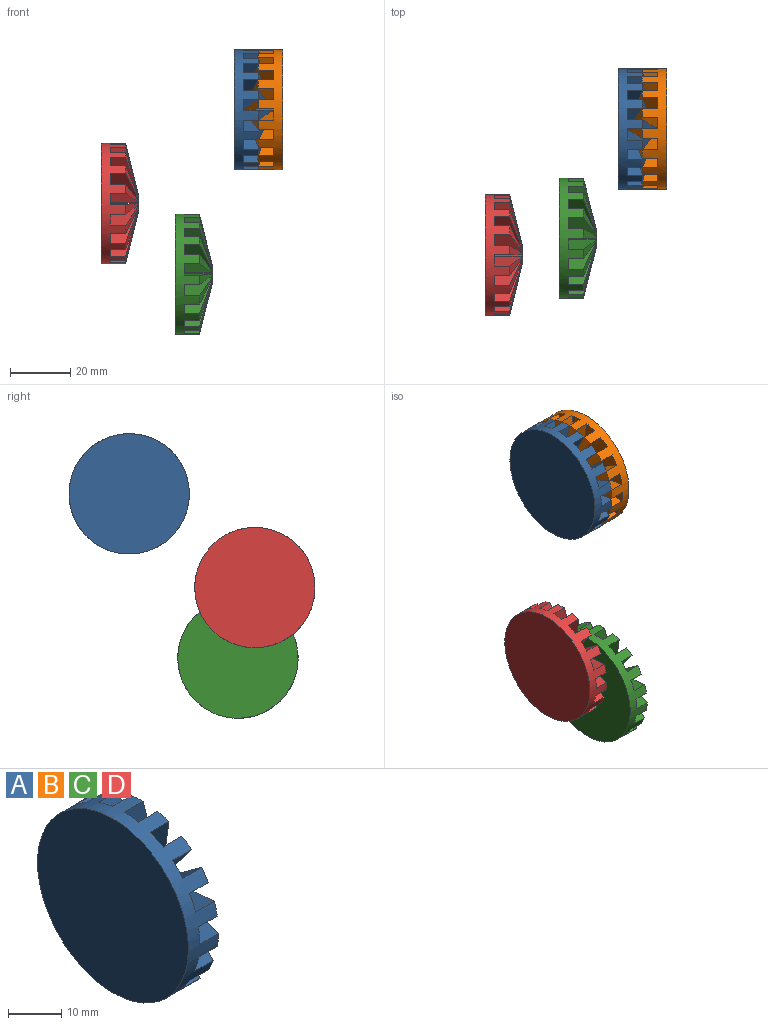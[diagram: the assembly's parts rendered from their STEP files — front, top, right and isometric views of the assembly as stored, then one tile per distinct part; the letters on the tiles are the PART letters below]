
ASSEMBLY  parts=4 mates=1
PART A: 75 faces, bbox 12.3x40x40 mm
  f0: cone r=0mm half-angle=76deg, axis (-1,0,0), area 31.7mm2, adj f18,f20,f21,f73
  f1: cone r=0mm half-angle=76deg, axis (-1,0,0), area 31.7mm2, adj f18,f22,f23,f24
  f2: cone r=0mm half-angle=76deg, axis (-1,0,0), area 31.7mm2, adj f18,f25,f26,f27
  f3: cone r=0mm half-angle=76deg, axis (-1,0,0), area 31.7mm2, adj f18,f28,f29,f30
  f4: cone r=0mm half-angle=76deg, axis (-1,0,0), area 31.7mm2, adj f18,f31,f32,f33
  f5: cone r=0mm half-angle=76deg, axis (-1,0,0), area 31.7mm2, adj f18,f34,f35,f36
  f6: cone r=0mm half-angle=76deg, axis (-1,0,0), area 31.7mm2, adj f18,f37,f38,f39
  f7: cone r=0mm half-angle=76deg, axis (-1,0,0), area 31.7mm2, adj f18,f40,f41,f42
  f8: cone r=0mm half-angle=76deg, axis (-1,0,0), area 31.7mm2, adj f18,f43,f44,f45
  f9: cone r=0mm half-angle=76deg, axis (-1,0,0), area 31.7mm2, adj f18,f46,f47,f48
  f10: cone r=0mm half-angle=76deg, axis (-1,0,0), area 31.7mm2, adj f18,f49,f50,f51
  f11: cone r=0mm half-angle=76deg, axis (-1,0,0), area 31.7mm2, adj f18,f52,f53,f54
  f12: cone r=0mm half-angle=76deg, axis (-1,0,0), area 31.7mm2, adj f18,f55,f56,f57
  f13: cone r=0mm half-angle=76deg, axis (-1,0,0), area 31.7mm2, adj f18,f58,f59,f60
  f14: cone r=0mm half-angle=76deg, axis (-1,0,0), area 31.7mm2, adj f18,f61,f62,f63
  f15: cone r=0mm half-angle=76deg, axis (-1,0,0), area 31.7mm2, adj f18,f64,f65,f66
  f16: cone r=0mm half-angle=76deg, axis (-1,0,0), area 31.7mm2, adj f18,f67,f68,f69
  f17: cone r=0mm half-angle=76deg, axis (-1,0,0), area 31.7mm2, adj f18,f70,f71,f72
  f18: cylinder r=20mm len=40mm, axis (-1,0,0), area 659.7mm2, adj f0,f1,f2,f3,f4,f5,f6,f7
  f19: plane 40x40mm, normal (-1,0,0), area 1256.6mm2, adj f18
  f20: cylinder r=3mm len=9.25mm, axis (-1,0,0), area 4.4mm2, adj f0,f21,f73,f74
  f21: plane 16.74x9.25mm, normal (0,-0.17,0.98), area 121.1mm2, adj f0,f18,f20,f74
  f22: plane 15.87x9.25mm, normal (0,0.36,-0.93), area 121.1mm2, adj f1,f18,f23,f74
  f23: cylinder r=3mm len=9.25mm, axis (-1,0,0), area 4.4mm2, adj f1,f22,f24,f74
  f24: plane 14.72x9.25mm, normal (0,-0.5,0.87), area 121.1mm2, adj f1,f18,f23,f74
  f25: plane 12.83x11.15mm, normal (0,0.66,-0.75), area 121.1mm2, adj f2,f18,f26,f74
  f26: cylinder r=3mm len=9.25mm, axis (-1,0,0), area 4.4mm2, adj f2,f25,f27,f74
  f27: plane 13.02x10.93mm, normal (0,-0.77,0.64), area 121.1mm2, adj f2,f18,f26,f74
  f28: plane 14.87x9.25mm, normal (0,0.87,-0.48), area 121.1mm2, adj f3,f18,f29,f74
  f29: cylinder r=3mm len=9.25mm, axis (-1,0,0), area 4.4mm2, adj f3,f28,f30,f74
  f30: plane 15.97x9.25mm, normal (0,-0.94,0.34), area 121.1mm2, adj f3,f18,f29,f74
  f31: plane 16.79x9.25mm, normal (0,0.99,-0.16), area 121.1mm2, adj f4,f18,f32,f74
  f32: cylinder r=3mm len=9.25mm, axis (-1,0,0), area 4.4mm2, adj f4,f31,f33,f74
  f33: plane 17x9.25mm, normal (0,-1,0), area 121.1mm2, adj f4,f18,f32,f74
  f34: plane 16.69x9.25mm, normal (0,0.98,0.19), area 121.1mm2, adj f5,f18,f35,f74
  f35: cylinder r=3mm len=9.25mm, axis (-1,0,0), area 4.4mm2, adj f5,f34,f36,f74
  f36: plane 15.97x9.25mm, normal (0,-0.94,-0.34), area 121.1mm2, adj f5,f18,f35,f74
  f37: plane 14.57x9.25mm, normal (0,0.86,0.52), area 121.1mm2, adj f6,f18,f38,f74
  f38: cylinder r=3mm len=9.25mm, axis (-1,0,0), area 4.4mm2, adj f6,f37,f39,f74
  f39: plane 13.02x10.93mm, normal (0,-0.77,-0.64), area 121.1mm2, adj f6,f18,f38,f74
  f40: plane 13.21x10.7mm, normal (0,0.63,0.78), area 121.1mm2, adj f7,f18,f41,f74
  f41: cylinder r=3mm len=9.25mm, axis (-1,0,0), area 4.4mm2, adj f7,f40,f42,f74
  f42: plane 14.72x9.25mm, normal (0,-0.5,-0.87), area 121.1mm2, adj f7,f18,f41,f74
  f43: plane 16.07x9.25mm, normal (0,0.33,0.95), area 121.1mm2, adj f8,f18,f44,f74
  f44: cylinder r=3mm len=9.25mm, axis (-1,0,0), area 4.4mm2, adj f8,f43,f45,f74
  f45: plane 16.74x9.25mm, normal (0,-0.17,-0.98), area 121.1mm2, adj f8,f18,f44,f74
  f46: plane 17x9.25mm, normal (0,-0.02,1), area 121.1mm2, adj f9,f18,f47,f74
  f47: cylinder r=3mm len=9.25mm, axis (-1,0,0), area 4.4mm2, adj f9,f46,f48,f74
  f48: plane 16.74x9.25mm, normal (0,0.17,-0.98), area 121.1mm2, adj f9,f18,f47,f74
  f49: plane 15.87x9.25mm, normal (0,-0.36,0.93), area 121.1mm2, adj f10,f18,f50,f74
  f50: cylinder r=3mm len=9.25mm, axis (-1,0,0), area 4.4mm2, adj f10,f49,f51,f74
  f51: plane 14.72x9.25mm, normal (0,0.5,-0.87), area 121.1mm2, adj f10,f18,f50,f74
  f52: plane 12.83x11.15mm, normal (0,-0.66,0.75), area 121.1mm2, adj f11,f18,f53,f74
  f53: cylinder r=3mm len=9.25mm, axis (-1,0,0), area 4.4mm2, adj f11,f52,f54,f74
  f54: plane 13.02x10.93mm, normal (0,0.77,-0.64), area 121.1mm2, adj f11,f18,f53,f74
  f55: plane 14.87x9.25mm, normal (0,-0.87,0.48), area 121.1mm2, adj f12,f18,f56,f74
  f56: cylinder r=3mm len=9.25mm, axis (-1,0,0), area 4.4mm2, adj f12,f55,f57,f74
  f57: plane 15.97x9.25mm, normal (0,0.94,-0.34), area 121.1mm2, adj f12,f18,f56,f74
  f58: plane 16.79x9.25mm, normal (0,-0.99,0.16), area 121.1mm2, adj f13,f18,f59,f74
  f59: cylinder r=3mm len=9.25mm, axis (-1,0,0), area 4.4mm2, adj f13,f58,f60,f74
  f60: plane 17x9.25mm, normal (0,1,0), area 121.1mm2, adj f13,f18,f59,f74
  f61: plane 16.69x9.25mm, normal (0,-0.98,-0.19), area 121.1mm2, adj f14,f18,f62,f74
  f62: cylinder r=3mm len=9.25mm, axis (-1,0,0), area 4.4mm2, adj f14,f61,f63,f74
  f63: plane 15.97x9.25mm, normal (0,0.94,0.34), area 121.1mm2, adj f14,f18,f62,f74
  f64: plane 14.57x9.25mm, normal (0,-0.86,-0.52), area 121.1mm2, adj f15,f18,f65,f74
  f65: cylinder r=3mm len=9.25mm, axis (-1,0,0), area 4.4mm2, adj f15,f64,f66,f74
  f66: plane 13.02x10.93mm, normal (0,0.77,0.64), area 121.1mm2, adj f15,f18,f65,f74
  f67: plane 13.21x10.7mm, normal (0,-0.63,-0.78), area 121.1mm2, adj f16,f18,f68,f74
  f68: cylinder r=3mm len=9.25mm, axis (-1,0,0), area 4.4mm2, adj f16,f67,f69,f74
  f69: plane 14.72x9.25mm, normal (0,0.5,0.87), area 121.1mm2, adj f16,f18,f68,f74
  f70: plane 16.07x9.25mm, normal (0,-0.33,-0.95), area 121.1mm2, adj f17,f18,f71,f74
  f71: cylinder r=3mm len=9.25mm, axis (-1,0,0), area 4.4mm2, adj f17,f70,f72,f74
  f72: plane 16.74x9.25mm, normal (0,0.17,0.98), area 121.1mm2, adj f17,f18,f71,f74
  f73: plane 17x9.25mm, normal (0,0.02,-1), area 121.1mm2, adj f0,f18,f20,f74
  f74: plane 40x40mm, normal (1,0,0), area 703.9mm2, adj f18,f20,f21,f22,f23,f24,f25,f26
PART B: same geometry as A
PART C: same geometry as A
PART D: same geometry as A
PLACE A t=(-3.24,0.12,0.28)mm fixed
PLACE B rot(axis=(0,1,0),180deg) t=(6.76,0.12,0.28)mm
PLACE C t=(-22.87,-36.07,-54.35)mm
PLACE D t=(-47.48,-41.7,-30.89)mm
MATE slider A.f0 <-> B.f0  axis (-1,0,0) through (-6.24,0.12,0.28)mm
